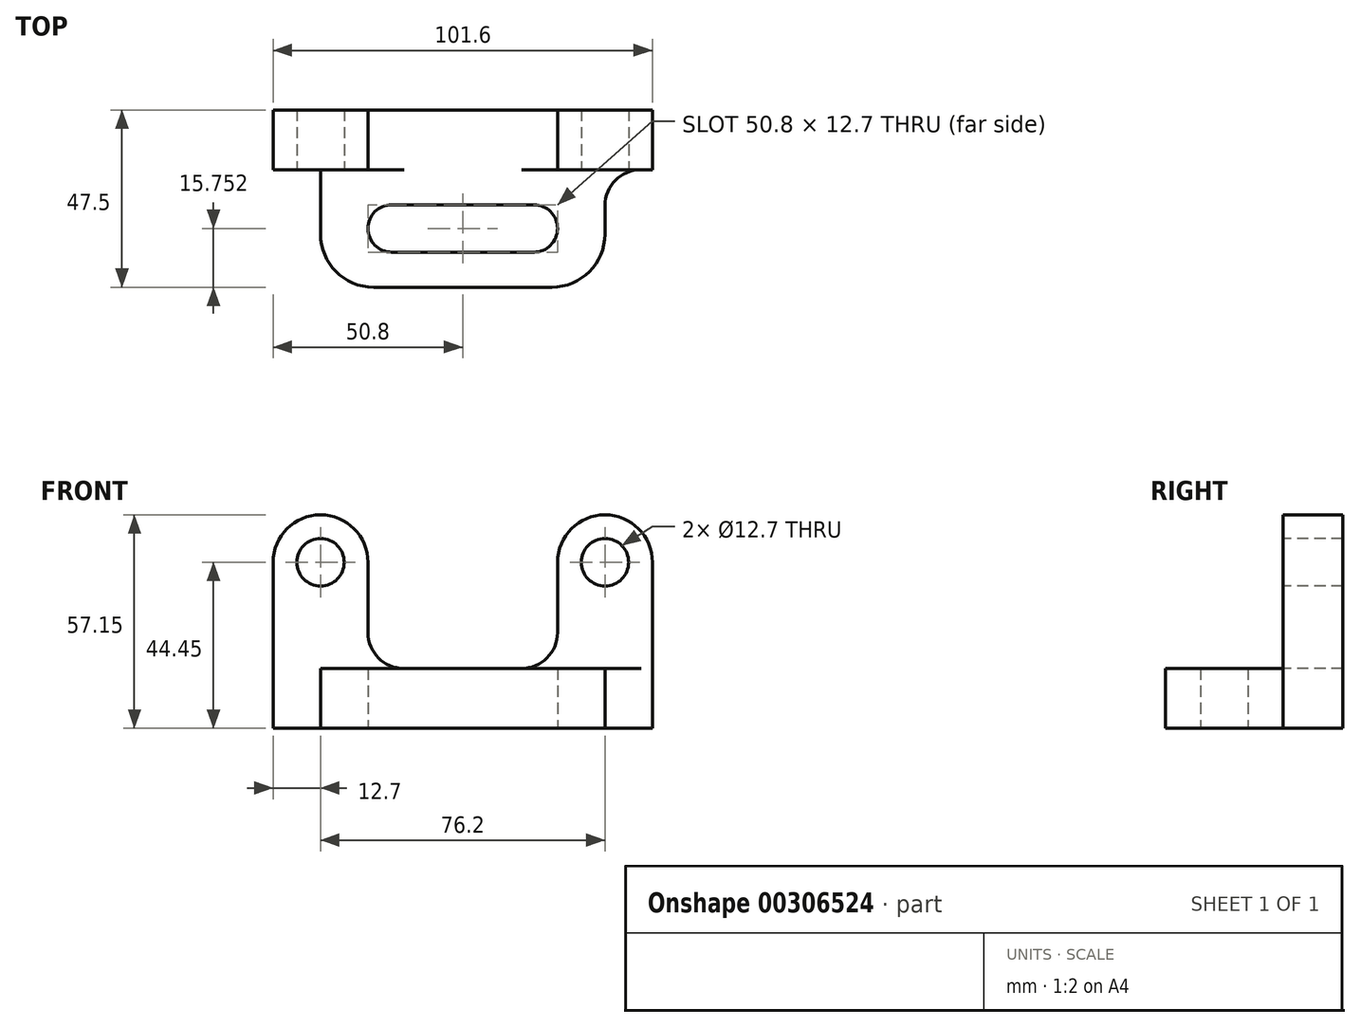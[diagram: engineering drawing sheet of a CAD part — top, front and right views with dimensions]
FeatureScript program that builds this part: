
annotation { "Feature Type Name" : "Feature", "Feature Type Description" : "" }
export const myFeature = defineFeature(function(context is Context, id is Id, definition is map)
    precondition{}
    {
        {
            var Q0;
            Q0=qCreatedBy(makeId("Front.planeOp"),FACE);
            var sketch = newSketch(context, id + "F0", { "sketchPlane" : qUnion([Q0])});
            skLineSegment(sketch, "E0", {"start": v(-50.8, 0) * mm, "end": v(50.8, 0) * mm});
            skLineSegment(sketch, "E1", {"start": v(-50.8, 0) * mm, "end": v(-50.8, 44.45) * mm});
            skLineSegment(sketch, "E2", {"start": v(50.8, 0) * mm, "end": v(50.8, 44.45) * mm});
            skArc(sketch, "E3", {"start": v(-25.4, 44.45) * mm, "mid": v(-38.1, 57.15) * mm, "end": v(-50.8, 44.45) * mm});
            skArc(sketch, "E4", {"start": v(50.8, 44.45) * mm, "mid": v(38.1, 57.15) * mm, "end": v(25.4, 44.45) * mm});
            skLineSegment(sketch, "E5", {"start": v(-25.4, 44.45) * mm, "end": v(-25.4, 16) * mm});
            skLineSegment(sketch, "E6", {"start": v(-25.4, 16) * mm, "end": v(25.4, 16) * mm});
            skLineSegment(sketch, "E7", {"start": v(25.4, 16) * mm, "end": v(25.4, 44.45) * mm});
            skCircle(sketch, "E8", {"center": v(-38.1, 44.45) * mm, "radius": 6.35 * mm});
            skCircle(sketch, "E9", {"center": v(38.1, 44.45) * mm, "radius": 6.35 * mm});
            skSolve(sketch);
        }
        {
            var Q0;
            Q0 = qSketchRegion(id + "F0", true);
            extrude(context, id + "F1", {"entities" : qUnion([Q0]), "oppositeDirection" : true, "depth" : 16 * mm});
        }
        {
            var Q0;
            Q0=makeQuery(id+"F1.opExtrude","SWEPT_EDGE",EDGE,{"disambiguationData":[OSD([sQuery(id+"F0.wireOp",EDGE,"E5"),sQuery(id+"F0.wireOp",EDGE,"E6")])]});
            var Q1;
            Q1=makeQuery(id+"F1.opExtrude","SWEPT_EDGE",EDGE,{"disambiguationData":[OSD([sQuery(id+"F0.wireOp",EDGE,"E6"),sQuery(id+"F0.wireOp",EDGE,"E7")])]});
            fillet(context, id + "F2", {"entities" : qUnion([Q0, Q1]), "radius" : 9.65 * mm, "tangentPropagation" : true, "allowEdgeOverflow" : false});
        }
        {
            var Q0;
            Q0=qCreatedBy(makeId("Top.planeOp"),FACE);
            var sketch = newSketch(context, id + "F3", { "sketchPlane" : qUnion([Q0])});
            skLineSegment(sketch, "E10.bottom", {"start": v(-38.1, 0) * mm, "end": v(38.1, 0) * mm});
            skLineSegment(sketch, "E10.top", {"start": v(-38.1, -31.5) * mm, "end": v(38.1, -31.5) * mm});
            skLineSegment(sketch, "E10.left", {"start": v(-38.1, 0) * mm, "end": v(-38.1, -31.5) * mm});
            skLineSegment(sketch, "E10.right", {"start": v(38.1, 0) * mm, "end": v(38.1, -31.5) * mm});
            skArc(sketch, "E11", {"start": v(-19.05, -9.4) * mm, "mid": v(-25.4, -15.75) * mm, "end": v(-19.05, -22.1) * mm});
            skArc(sketch, "E12", {"start": v(19.05, -22.1) * mm, "mid": v(25.4, -15.75) * mm, "end": v(19.05, -9.4) * mm});
            skLineSegment(sketch, "E13", {"start": v(-19.05, -9.4) * mm, "end": v(19.05, -9.4) * mm});
            skLineSegment(sketch, "E14", {"start": v(19.05, -22.1) * mm, "end": v(-19.05, -22.1) * mm});
            skLineSegment(sketch, "E15", {"start": v(-38.1, -15.75) * mm, "end": v(76.2, -15.75) * mm, "construction": true});
            skSolve(sketch);
        }
        {
            var Q0;
            Q0 = qSketchRegion(id + "F3", true);
            extrude(context, id + "F4", {"entities" : qUnion([Q0]), "operationType" : NewBodyOperationType.ADD, "depth" : 16 * mm});
        }
        {
            var Q0;
            Q0=makeQuery(id+"F4.opExtrude","SWEPT_EDGE",EDGE,{"disambiguationData":[OSD([sQuery(id+"F3.wireOp",EDGE,"E10.top"),sQuery(id+"F3.wireOp",EDGE,"E10.right")])]});
            var Q1;
            Q1=makeQuery(id+"F4.opExtrude","SWEPT_EDGE",EDGE,{"disambiguationData":[OSD([sQuery(id+"F3.wireOp",EDGE,"E10.top"),sQuery(id+"F3.wireOp",EDGE,"E10.left")])]});
            fillet(context, id + "F5", {"entities" : qUnion([Q0, Q1]), "radius" : 14.22 * mm, "tangentPropagation" : true, "allowEdgeOverflow" : false});
        }
        {
            var Q0;
            Q0=makeQuery(id+"F4.opExtrude","SWEPT_EDGE",EDGE,{"disambiguationData":[OSD([sQuery(id+"F3.wireOp",EDGE,"E10.bottom"),sQuery(id+"F3.wireOp",EDGE,"E10.right")])]});
            var Q1;
            Q1=makeQuery(id+"F4.opExtrude","SWEPT_EDGE",EDGE,{"disambiguationData":[OSD([sQuery(id+"F3.wireOp",EDGE,"E10.bottom"),sQuery(id+"F3.wireOp",EDGE,"E10.left")])]});
            fillet(context, id + "F6", {"entities" : qUnion([Q0, Q1]), "radius" : 9.65 * mm, "tangentPropagation" : true, "allowEdgeOverflow" : false});
        }
    });
